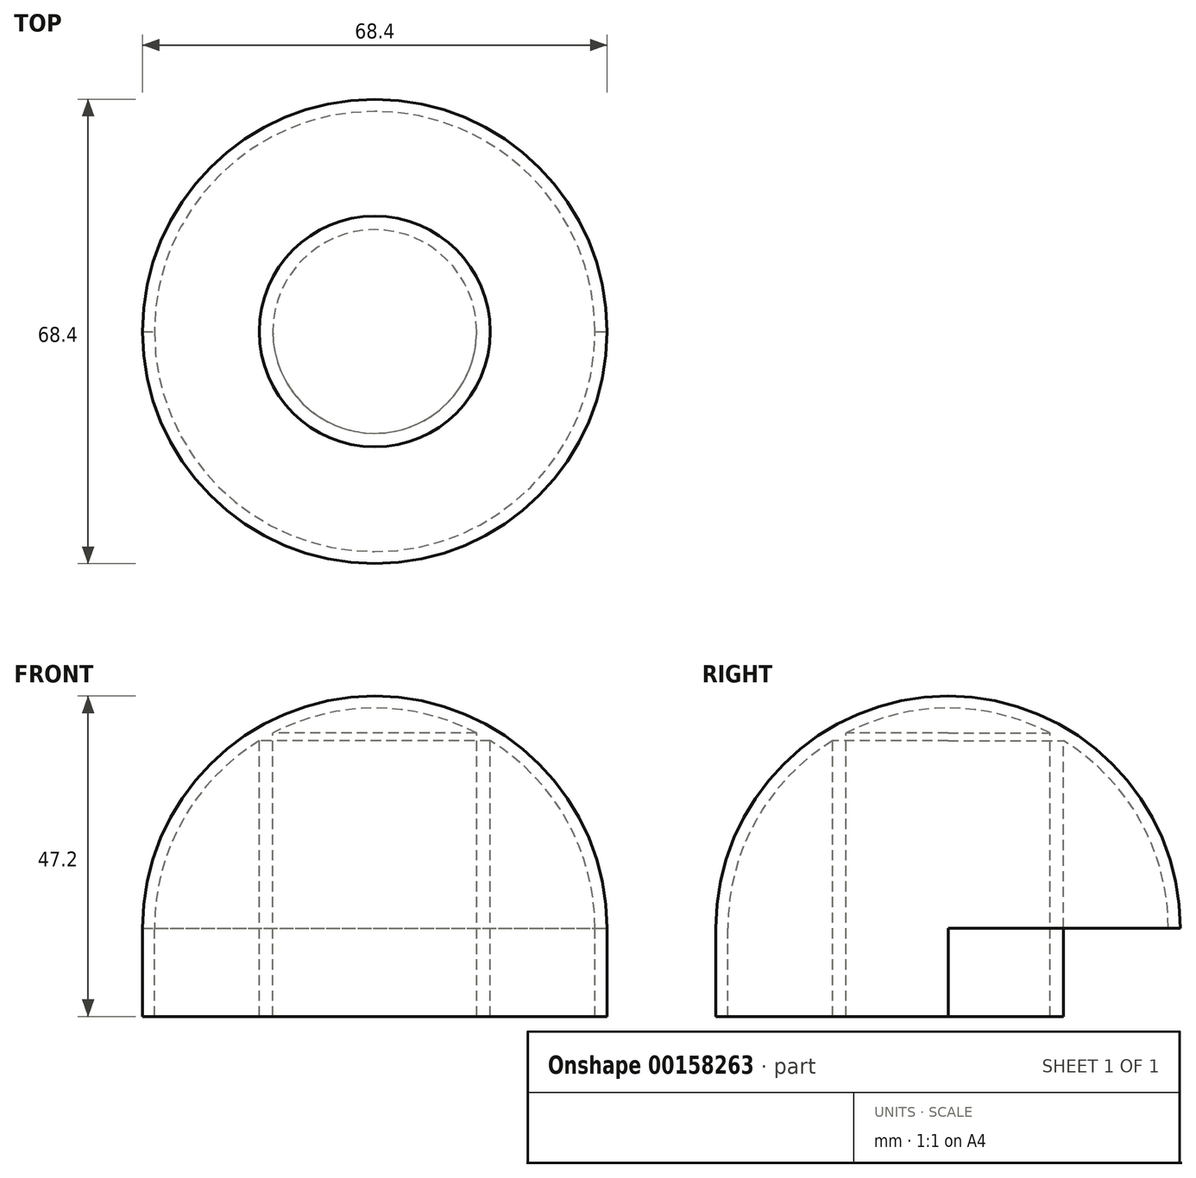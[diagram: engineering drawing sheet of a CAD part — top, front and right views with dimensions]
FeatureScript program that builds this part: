
annotation { "Feature Type Name" : "Feature", "Feature Type Description" : "" }
export const myFeature = defineFeature(function(context is Context, id is Id, definition is map)
    precondition{}
    {
        {
            var Q0;
            Q0=qCreatedBy(makeId("Top.planeOp"),FACE);
            var sketch = newSketch(context, id + "F0", { "sketchPlane" : qUnion([Q0])});
            skCircle(sketch, "E0", {"center": v(0, 0) * mm, "radius": 15 * mm});
            skCircle(sketch, "E1", {"center": v(0, 0) * mm, "radius": 17 * mm});
            skArc(sketch, "E2", {"start": v(-32.43, 0) * mm, "mid": v(0, -32.43) * mm, "end": v(32.43, 0) * mm});
            skLineSegment(sketch, "E3", {"start": v(-48.8, 0) * mm, "end": v(64.86, 0) * mm});
            skArc(sketch, "E4", {"start": v(-34.2, 0) * mm, "mid": v(0, -34.2) * mm, "end": v(34.2, 0) * mm});
            skArc(sketch, "E5.MirrorCS", {"start": v(-34.2, 0) * mm, "mid": v(0, 34.2) * mm, "end": v(34.2, 0) * mm});
            skArc(sketch, "E6.MirrorCS", {"start": v(-32.43, 0) * mm, "mid": v(0, 32.43) * mm, "end": v(32.43, 0) * mm});
            skSolve(sketch);
        }
        {
            var Q0;
            {var subQ3=sQuery(id+"F0.wireOp",EDGE,"E5.MirrorCS");Q0=makeQuery(id+"F0.imprint","IMPRINT",FACE,{"disambiguationData":[TD([[makeQuery(id+"F0.imprint","IMPRINT",EDGE,{"derivedFrom":subQ3}),-1.0]])]});}
            var Q1;
            {var subQ0=sQuery(id+"F0.wireOp",EDGE,"E3");var subQ1=sQuery(id+"F0.wireOp",EDGE,"E0");var subQ2=makeQuery(id+"F0.imprint","INTERSECT",VERTEX,{"disambiguationData":[OD(0.0)],"derivedFrom":[subQ1,subQ0]});Q1=makeQuery(id+"F0.imprint","IMPRINT",FACE,{"disambiguationData":[TD([[makeQuery(id+"F0.imprint","IMPRINT",EDGE,{"disambiguationData":[TD([[subQ2,1.0]])],"derivedFrom":subQ1}),-1.0]])]});}
            var Q2;
            {var subQ0=sQuery(id+"F0.wireOp",EDGE,"E3");var subQ1=sQuery(id+"F0.wireOp",EDGE,"E0");var subQ2=makeQuery(id+"F0.imprint","INTERSECT",VERTEX,{"disambiguationData":[OD(0.0)],"derivedFrom":[subQ1,subQ0]});Q2=makeQuery(id+"F0.imprint","IMPRINT",FACE,{"disambiguationData":[TD([[makeQuery(id+"F0.imprint","IMPRINT",EDGE,{"disambiguationData":[TD([[subQ2,-1.0]])],"derivedFrom":subQ1}),-1.0]])]});}
            var Q3;
            {var subQ0=sQuery(id+"F0.wireOp",EDGE,"E2");Q3=makeQuery(id+"F0.imprint","IMPRINT",FACE,{"disambiguationData":[TD([[makeQuery(id+"F0.imprint","IMPRINT",EDGE,{"derivedFrom":subQ0}),-1.0]])]});}
            extrude(context, id + "F1", {"entities" : qUnion([Q0, Q1, Q2, Q3]), "oppositeDirection" : true, "depth" : 13 * mm});
        }
        {
            var Q0;
            Q0=sQuery(id+"F0.wireOp",EDGE,"E3");
            extrude(context, id + "F2", {"bodyType" : ExtendedToolBodyType.SURFACE, "surfaceEntities" : qUnion([Q0]), "depth" : 0.01 * mm});
        }
        {
            var Q0;
            {var subQ0=sQuery(id+"F0.wireOp",EDGE,"E2");Q0=makeQuery(id+"F0.imprint","IMPRINT",FACE,{"disambiguationData":[TD([[makeQuery(id+"F0.imprint","IMPRINT",EDGE,{"derivedFrom":subQ0}),-1.0]])]});}
            var Q1;
            Q1=makeQuery(id+"F2.opExtrude","CAP_EDGE",EDGE,{"disambiguationData":[OSD([sQuery(id+"F0.wireOp",EDGE,"E3")])],"isStart":true});
            revolve(context, id + "F3", {"operationType" : NewBodyOperationType.ADD, "entities" : qUnion([Q0]), "axis" : qUnion([Q1]), "revolveType" : RevolveType.ONE_DIRECTION, "oppositeDirection" : true, "angle" : 180 * degree});
        }
        {
            var Q0;
            Q0=makeQuery(id+"F0.imprint","IMPRINT",FACE,{"disambiguationData":[TD([[makeQuery(id+"F0.imprint","IMPRINT",EDGE,{"derivedFrom":sQuery(id+"F0.wireOp",EDGE,"E0")}),-1.0]])]});
            extrude(context, id + "F4", {"entities" : qUnion([Q0]), "operationType" : NewBodyOperationType.ADD, "depth" : 29.5 * mm});
        }
    });
